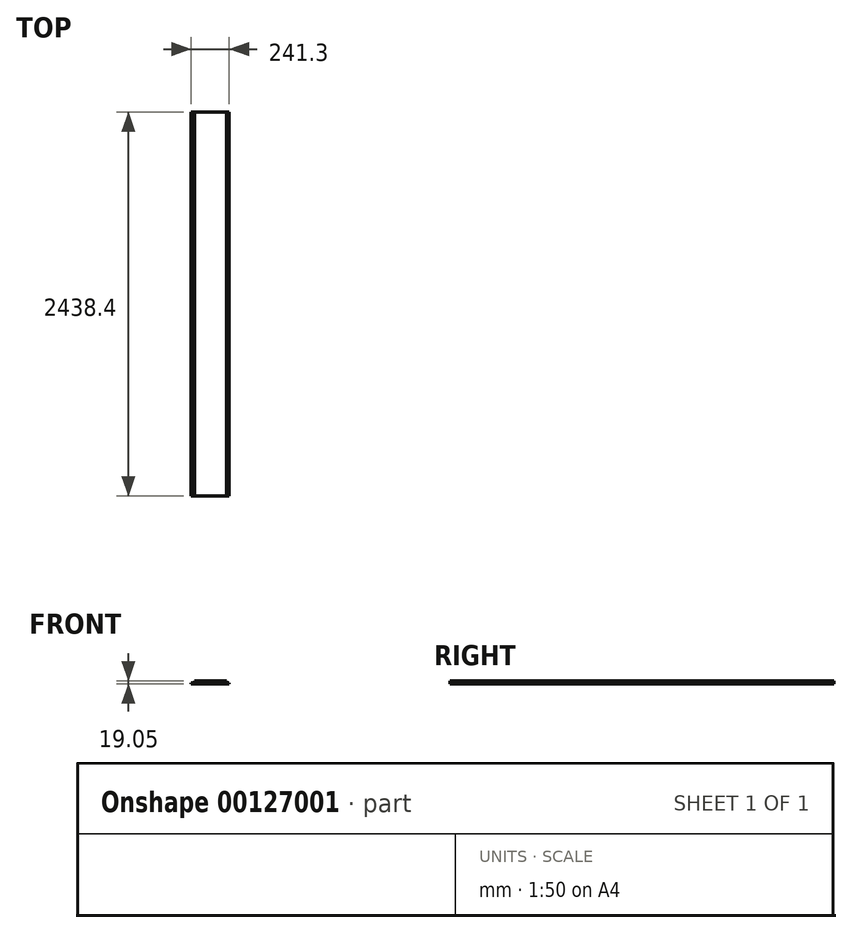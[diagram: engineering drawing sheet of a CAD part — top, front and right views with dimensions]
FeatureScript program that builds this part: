
annotation { "Feature Type Name" : "Feature", "Feature Type Description" : "" }
export const myFeature = defineFeature(function(context is Context, id is Id, definition is map)
    precondition{}
    {
        {
            var Q0;
            Q0=qCreatedBy(makeId("Front.planeOp"),FACE);
            var sketch = newSketch(context, id + "F0", { "sketchPlane" : qUnion([Q0])});
            skLineSegment(sketch, "E0", {"start": v(-87.26, 25.72) * mm, "end": v(115.94, 25.72) * mm});
            skLineSegment(sketch, "E1", {"start": v(-87.26, 25.72) * mm, "end": v(-87.26, 13.02) * mm});
            skLineSegment(sketch, "E2", {"start": v(115.94, 25.72) * mm, "end": v(115.94, 13.02) * mm});
            skLineSegment(sketch, "E3", {"start": v(115.94, 13.02) * mm, "end": v(-87.26, 13.02) * mm});
            skLineSegment(sketch, "E4", {"start": v(-87.26, 13.02) * mm, "end": v(-106.3, 13.02) * mm});
            skLineSegment(sketch, "E5", {"start": v(-106.3, 13.02) * mm, "end": v(-106.3, 6.67) * mm});
            skLineSegment(sketch, "E6", {"start": v(115.94, 13.02) * mm, "end": v(135, 13.02) * mm});
            skLineSegment(sketch, "E7", {"start": v(135, 13.02) * mm, "end": v(135, 6.67) * mm});
            skLineSegment(sketch, "E8", {"start": v(135, 6.67) * mm, "end": v(-106.3, 6.67) * mm});
            skSolve(sketch);
        }
        {
            var Q0;
            Q0 = qSketchRegion(id + "F0", true);
            extrude(context, id + "F1", {"entities" : qUnion([Q0]), "oppositeDirection" : true, "depth" : 2438.4 * mm});
        }
    });
